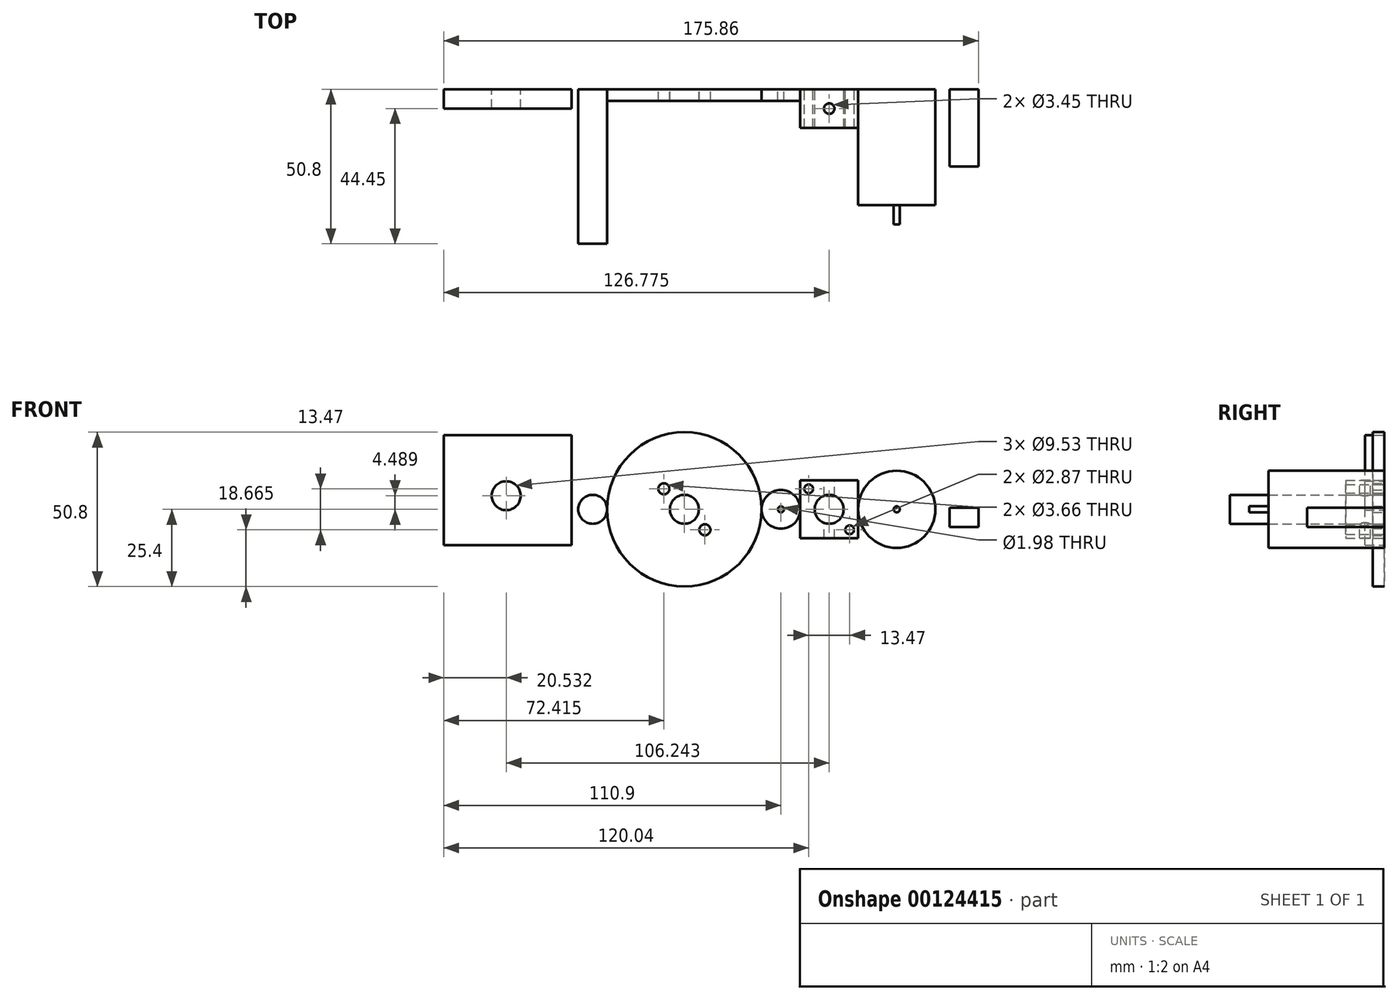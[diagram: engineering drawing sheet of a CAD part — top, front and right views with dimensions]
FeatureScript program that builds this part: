
annotation { "Feature Type Name" : "Feature", "Feature Type Description" : "" }
export const myFeature = defineFeature(function(context is Context, id is Id, definition is map)
    precondition{}
    {
        {
            var Q0;
            Q0=qCreatedBy(makeId("Front.planeOp"),FACE);
            var sketch = newSketch(context, id + "F0", { "sketchPlane" : qUnion([Q0])});
            skCircle(sketch, "E0", {"center": v(0, 0) * mm, "radius": 1 * mm});
            skCircle(sketch, "E1", {"center": v(0, 0) * mm, "radius": 6.35 * mm});
            skCircle(sketch, "E2", {"center": v(-31.75, 0) * mm, "radius": 25.4 * mm});
            skPoint(sketch, "E2.first.point", {"position": v(-6.35, 0) * mm});
            skPoint(sketch, "E2.second.point", {"position": v(-57.15, 0) * mm});
            skPoint(sketch, "E2.third.point", {"position": v(-24.55, 24.36) * mm});
            skCircle(sketch, "E3", {"center": v(-31.75, 0) * mm, "radius": 4.76 * mm});
            skLineSegment(sketch, "E4.bottom", {"start": v(6.35, 9.53) * mm, "end": v(25.4, 9.53) * mm});
            skLineSegment(sketch, "E4.top", {"start": v(6.35, -9.52) * mm, "end": v(25.4, -9.52) * mm});
            skLineSegment(sketch, "E4.left", {"start": v(6.35, 9.53) * mm, "end": v(6.35, -9.53) * mm});
            skLineSegment(sketch, "E4.right", {"start": v(25.4, 9.53) * mm, "end": v(25.4, -9.52) * mm});
            skPoint(sketch, "E4.middle", {"position": v(15.87, 0) * mm});
            skLineSegment(sketch, "E5", {"start": v(15.88, 0) * mm, "end": v(15.87, 9.53) * mm, "construction": true});
            skCircle(sketch, "E6.MirrorC", {"center": v(9.14, 6.74) * mm, "radius": 1.44 * mm});
            skLineSegment(sketch, "E7", {"start": v(-31.75, 0) * mm, "end": v(-22.23, 0) * mm, "construction": true});
            skLineSegment(sketch, "E8", {"start": v(-31.75, 0) * mm, "end": v(-31.75, 25.4) * mm, "construction": true});
            skCircle(sketch, "E9", {"center": v(15.87, 0) * mm, "radius": 4.76 * mm});
            skLineSegment(sketch, "E10", {"start": v(9.14, 6.74) * mm, "end": v(22.61, -6.74) * mm, "construction": true});
            skCircle(sketch, "E11", {"center": v(22.61, -6.74) * mm, "radius": 1.44 * mm});
            skCircle(sketch, "E12", {"center": v(38.1, 0) * mm, "radius": 12.7 * mm});
            skLineSegment(sketch, "E13", {"start": v(15.87, 0) * mm, "end": v(38.1, 0) * mm});
            skLineSegment(sketch, "E14.bottom", {"start": v(55.43, -5.76) * mm, "end": v(64.96, -5.76) * mm});
            skLineSegment(sketch, "E14.top", {"start": v(55.43, 0.6) * mm, "end": v(64.96, 0.6) * mm});
            skLineSegment(sketch, "E14.left", {"start": v(55.43, -5.76) * mm, "end": v(55.43, 0.6) * mm});
            skLineSegment(sketch, "E14.right", {"start": v(64.96, -5.76) * mm, "end": v(64.96, 0.6) * mm});
            skCircle(sketch, "E15", {"center": v(-61.91, 0) * mm, "radius": 4.76 * mm});
            skLineSegment(sketch, "E16.bottom", {"start": v(-68.89, -11.74) * mm, "end": v(-110.9, -11.74) * mm});
            skLineSegment(sketch, "E16.top", {"start": v(-68.89, 24.4) * mm, "end": v(-110.9, 24.4) * mm});
            skLineSegment(sketch, "E16.left", {"start": v(-68.89, -11.74) * mm, "end": v(-68.89, 24.4) * mm});
            skLineSegment(sketch, "E16.right", {"start": v(-110.9, -11.74) * mm, "end": v(-110.9, 24.4) * mm});
            skCircle(sketch, "E17", {"center": v(-90.37, 4.49) * mm, "radius": 4.76 * mm});
            skLineSegment(sketch, "E18", {"start": v(-31.75, 0) * mm, "end": v(-38.49, 6.74) * mm, "construction": true});
            skCircle(sketch, "E19", {"center": v(-38.49, 6.74) * mm, "radius": 1.83 * mm});
            skLineSegment(sketch, "E20", {"start": v(-31.75, 0) * mm, "end": v(-25.54, 6.2) * mm, "construction": true});
            skLineSegment(sketch, "E21.MirrorCS", {"start": v(-31.75, 0) * mm, "end": v(-25.01, -6.74) * mm, "construction": true});
            skCircle(sketch, "E22.MirrorC", {"center": v(-25.01, -6.74) * mm, "radius": 1.83 * mm});
            skSolve(sketch);
        }
        {
            var Q0;
            Q0=makeQuery(id+"F0.imprint","IMPRINT",FACE,{"disambiguationData":[TD([[makeQuery(id+"F0.imprint","IMPRINT",EDGE,{"derivedFrom":sQuery(id+"F0.wireOp",EDGE,"E2")}),1.0]])]});
            var Q1;
            Q1=makeQuery(id+"F0.imprint","IMPRINT",FACE,{"disambiguationData":[TD([[makeQuery(id+"F0.imprint","IMPRINT",EDGE,{"derivedFrom":sQuery(id+"F0.wireOp",EDGE,"E0")}),-1.0]])]});
            extrude(context, id + "F1", {"entities" : qUnion([Q0, Q1]), "depth" : 3.8 * mm});
        }
        {
            var Q0;
            {var subQ3=sQuery(id+"F0.wireOp",EDGE,"E4.bottom");Q0=makeQuery(id+"F0.imprint","IMPRINT",FACE,{"disambiguationData":[TD([[makeQuery(id+"F0.imprint","IMPRINT",EDGE,{"derivedFrom":subQ3}),-1.0]])]});}
            extrude(context, id + "F2", {"entities" : qUnion([Q0]), "operationType" : NewBodyOperationType.ADD, "depth" : 12.7 * mm});
        }
        {
            var Q0;
            Q0=makeQuery(id+"F0.imprint","IMPRINT",FACE,{"disambiguationData":[TD([[makeQuery(id+"F0.imprint","IMPRINT",EDGE,{"derivedFrom":sQuery(id+"F0.wireOp",EDGE,"E12")}),1.0]])]});
            extrude(context, id + "F3", {"entities" : qUnion([Q0]), "operationType" : NewBodyOperationType.ADD, "depth" : 38.1 * mm});
        }
        {
            var Q0;
            Q0=makeQuery(id+"F3.opExtrude","CAP_FACE",FACE,{"disambiguationData":[OSD([sQuery(id+"F0.wireOp",EDGE,"E12")])],"isStart":false});
            var sketch = newSketch(context, id + "F4", { "sketchPlane" : qUnion([Q0])});
            skCircle(sketch, "E23", {"center": v(38.1, 0) * mm, "radius": 1 * mm});
            skSolve(sketch);
        }
        {
            var Q0;
            Q0=makeQuery(id+"F4.imprint","IMPRINT",FACE,{"disambiguationData":[TD([[makeQuery(id+"F4.imprint","IMPRINT",EDGE,{"derivedFrom":sQuery(id+"F4.wireOp",EDGE,"E23")}),1.0]])]});
            extrude(context, id + "F5", {"entities" : qUnion([Q0]), "operationType" : NewBodyOperationType.ADD, "depth" : 6.35 * mm});
        }
        {
            var Q0;
            Q0=makeQuery(id+"F0.imprint","IMPRINT",FACE,{"disambiguationData":[TD([[makeQuery(id+"F0.imprint","IMPRINT",EDGE,{"derivedFrom":sQuery(id+"F0.wireOp",EDGE,"E14.bottom")}),1.0]])]});
            extrude(context, id + "F6", {"entities" : qUnion([Q0]), "depth" : 25.4 * mm});
        }
        {
            var Q0;
            Q0=makeQuery(id+"F2.opExtrude","SWEPT_FACE",FACE,{"disambiguationData":[OSD([sQuery(id+"F0.wireOp",EDGE,"E4.bottom")])]});
            var sketch = newSketch(context, id + "F7", { "sketchPlane" : qUnion([Q0])});
            skCircle(sketch, "E24", {"center": v(15.88, -6.35) * mm, "radius": 1.73 * mm});
            skPoint(sketch, "E25.start.orphan", {"position": v(6.35, -6.35) * mm});
            skPoint(sketch, "E26.trimOffspring.end.orphan", {"position": v(25.4, -6.35) * mm});
            skSolve(sketch);
        }
        {
            var Q0;
            Q0=makeQuery(id+"F7.imprint","IMPRINT",FACE,{"disambiguationData":[TD([[makeQuery(id+"F7.imprint","IMPRINT",EDGE,{"derivedFrom":sQuery(id+"F7.wireOp",EDGE,"E24")}),1.0]])]});
            extrude(context, id + "F8", {"entities" : qUnion([Q0]), "operationType" : NewBodyOperationType.REMOVE, "endBound" : BoundingType.THROUGH_ALL, "oppositeDirection" : true, "depth" : 25.4 * mm});
        }
        {
            var Q0;
            Q0=makeQuery(id+"F0.imprint","IMPRINT",FACE,{"disambiguationData":[TD([[makeQuery(id+"F0.imprint","IMPRINT",EDGE,{"derivedFrom":sQuery(id+"F0.wireOp",EDGE,"E15")}),1.0]])]});
            extrude(context, id + "F9", {"entities" : qUnion([Q0]), "operationType" : NewBodyOperationType.ADD, "depth" : 50.8 * mm});
        }
        {
            var Q0;
            Q0=makeQuery(id+"F0.imprint","IMPRINT",FACE,{"disambiguationData":[TD([[makeQuery(id+"F0.imprint","IMPRINT",EDGE,{"derivedFrom":sQuery(id+"F0.wireOp",EDGE,"E16.bottom")}),-1.0]])]});
            extrude(context, id + "F10", {"entities" : qUnion([Q0]), "depth" : 6.35 * mm});
        }
    });
